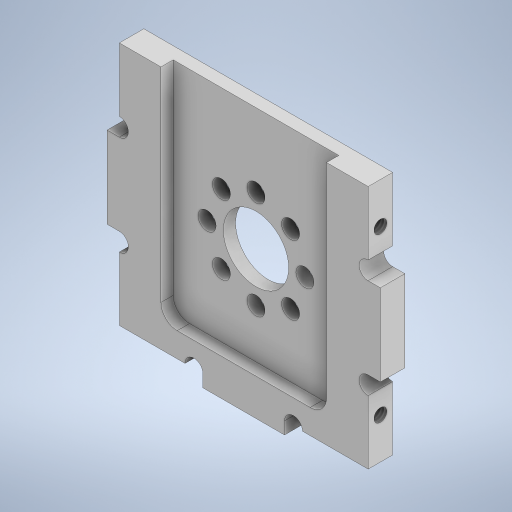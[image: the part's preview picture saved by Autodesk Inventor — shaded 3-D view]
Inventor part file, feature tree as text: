
AUTODESK INVENTOR PART (.ipt)
format: ipt  version: 2024 (Build 280153000, 153)  size: 347,136 bytes
history: native  units: mm
features: extrude x5, sketch x5, hole x2, other x1, fillet x1
ambient origin geometry x8: Origin, YZ Plane, XZ Plane, XY Plane, X Axis, Y Axis, Z Axis, Center Point
bodies: Body1 (feature_tree)
feature tree (14):
  other  "ソリッド1"
  extrude  "押し出し1"  Depth=1.5mm
  hole  "穴1"  [1 undecoded]
  extrude  "押し出し2"  Depth=30.5mm
  sketch  "スケッチ4"
  extrude  "押し出し3"  Depth=30.0mm
  hole  "穴2"  [1 undecoded]
  extrude  "押し出し4"  Depth=3.0mm TaperAngle=0.0deg
  extrude  "押し出し5"  Depth=5.0mm
  fillet  "フィレット1"  Radius=5.0mm
  sketch  "スケッチ1"
  sketch  "スケッチ2"
  sketch  "スケッチ3"
  sketch  "スケッチ5"
note: 2 required parameter values undecoded (feature->parameter linkage not recoverable at this tier; creation-order binding heuristic only, values carry confidence <= 0.55)
